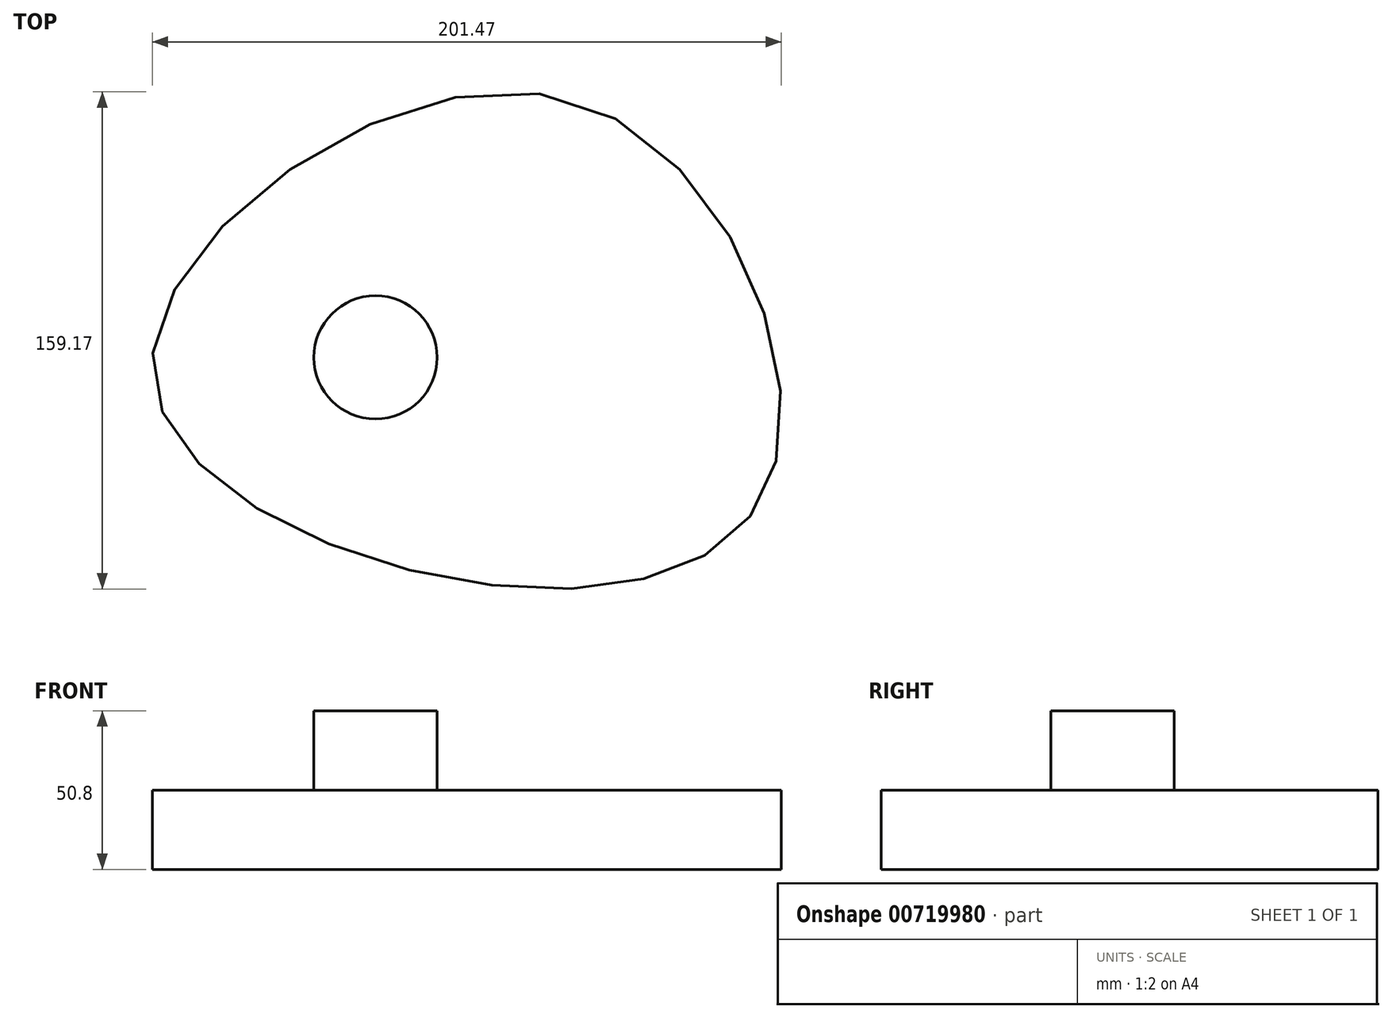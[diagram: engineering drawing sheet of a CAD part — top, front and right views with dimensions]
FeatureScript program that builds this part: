
annotation { "Feature Type Name" : "Feature", "Feature Type Description" : "" }
export const myFeature = defineFeature(function(context is Context, id is Id, definition is map)
    precondition{}
    {
        {
            var Q0;
            Q0=qCreatedBy(makeId("Top.planeOp"),FACE);
            var sketch = newSketch(context, id + "F0", { "sketchPlane" : qUnion([Q0])});
            skFitSpline(sketch, "E0", {"points": [v(-97.11, 20.64) * mm, v(33.8, 102.4) * mm, v(101.36, -18.18) * mm, v(0, -52.04) * mm, v(-97.11, 20.64) * mm]});
            skSolve(sketch);
        }
        {
            var Q0;
            Q0 = qSketchRegion(id + "F0", true);
            extrude(context, id + "F1", {"entities" : qUnion([Q0]), "depth" : 25.4 * mm, "offsetDistance" : 25.4 * mm});
        }
        {
            var Q0;
            Q0=makeQuery(id+"F1.opExtrude","CAP_FACE",FACE,{"disambiguationData":[OSD([sQuery(id+"F0.wireOp",EDGE,"E0")])],"isStart":false});
            var sketch = newSketch(context, id + "F2", { "sketchPlane" : qUnion([Q0])});
            skCircle(sketch, "E1", {"center": v(-25.79, 19.25) * mm, "radius": 19.74 * mm});
            skSolve(sketch);
        }
        {
            var Q0;
            Q0 = qSketchRegion(id + "F2", true);
            extrude(context, id + "F3", {"entities" : qUnion([Q0]), "operationType" : NewBodyOperationType.ADD, "depth" : 25.4 * mm, "offsetDistance" : 25.4 * mm});
        }
    });
